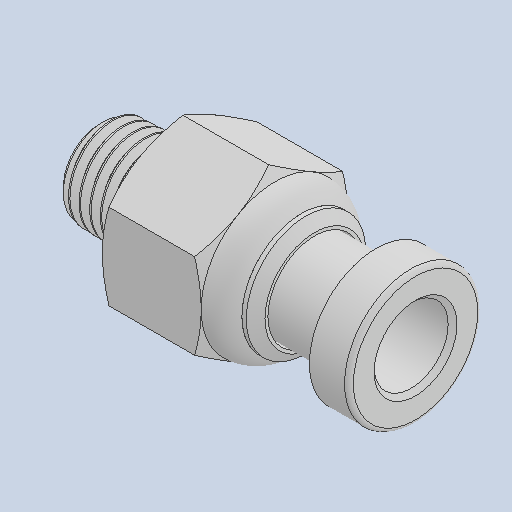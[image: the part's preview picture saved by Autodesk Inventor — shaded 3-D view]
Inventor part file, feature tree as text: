
AUTODESK INVENTOR PART (.ipt)
format: ipt  version: 2022 (Build 260153000, 153)  size: 654,336 bytes
history: native  units: in
note: dims shown in document units (in); Inventor stores cm internally (conversion verified against a paired STEP export)
features: revolve x3, fillet x1, other x1
ambient origin geometry x8: Origin, YZ Plane, XZ Plane, XY Plane, X Axis, Y Axis, Z Axis, Center Point
bodies: Solid1 (feature_tree), Solid2 (feature_tree), Solid3 (feature_tree), Solid4 (feature_tree), Solid5 (feature_tree)
feature tree (5):
  fillet  "Fillet1"  [1 undecoded]
  other  "Cut-Revolve3"
  revolve  "Revolve3"  [1 undecoded]
  revolve  "Revolve4"  [1 undecoded]
  revolve  "Revolve5"  [1 undecoded]
note: 4 required parameter values undecoded (feature->parameter linkage not recoverable at this tier; creation-order binding heuristic only, values carry confidence <= 0.55)
